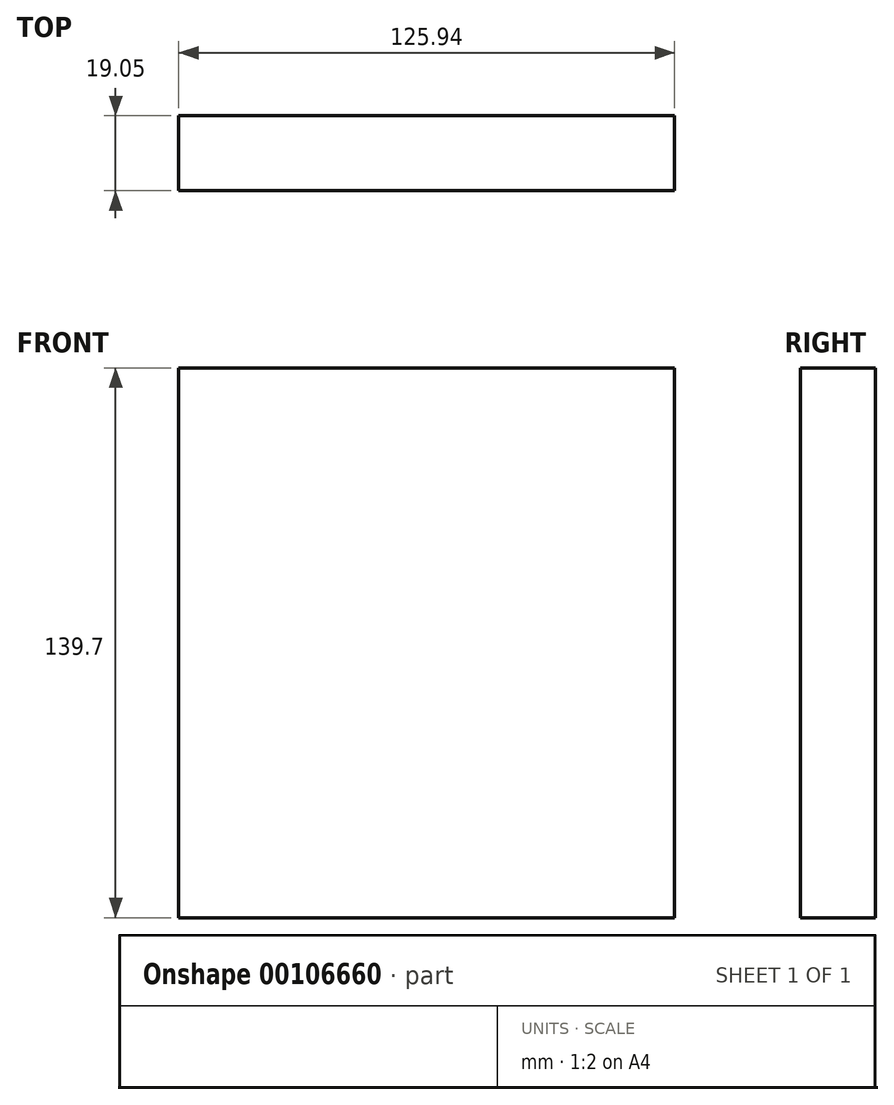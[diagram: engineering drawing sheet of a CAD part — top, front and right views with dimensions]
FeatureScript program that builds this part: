
annotation { "Feature Type Name" : "Feature", "Feature Type Description" : "" }
export const myFeature = defineFeature(function(context is Context, id is Id, definition is map)
    precondition{}
    {
        {
            var Q0;
            Q0=qCreatedBy(makeId("Front.planeOp"),FACE);
            var sketch = newSketch(context, id + "F0", { "sketchPlane" : qUnion([Q0])});
            skLineSegment(sketch, "E0.bottom", {"start": v(0, 0) * mm, "end": v(125.94, 0) * mm});
            skLineSegment(sketch, "E0.top", {"start": v(0, 139.7) * mm, "end": v(125.94, 139.7) * mm});
            skLineSegment(sketch, "E0.left", {"start": v(0, 0) * mm, "end": v(0, 139.7) * mm});
            skLineSegment(sketch, "E0.right", {"start": v(125.94, 0) * mm, "end": v(125.94, 139.7) * mm});
            skSolve(sketch);
        }
        {
            var Q0;
            Q0=makeQuery(id+"F0.imprint","IMPRINT",FACE,{"disambiguationData":[TD([[makeQuery(id+"F0.imprint","IMPRINT",EDGE,{"derivedFrom":sQuery(id+"F0.wireOp",EDGE,"E0.bottom")}),1.0]])]});
            extrude(context, id + "F1", {"entities" : qUnion([Q0]), "depth" : 19.05 * mm});
        }
    });
